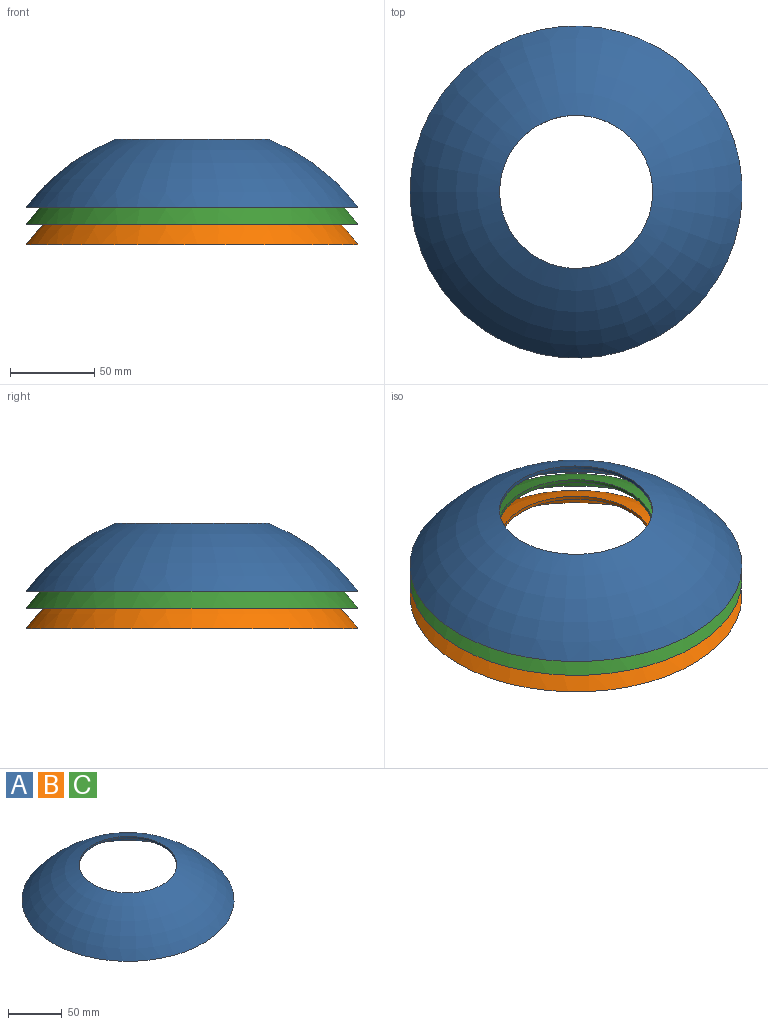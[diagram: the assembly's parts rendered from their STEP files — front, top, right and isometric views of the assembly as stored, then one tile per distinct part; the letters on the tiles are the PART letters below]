
ASSEMBLY  parts=3 mates=1
PART A: 4 faces, bbox 197.5x197.5x40.5 mm
  f0: cylinder r=45.5mm len=91mm, axis (0,0,-1), area 614.7mm2, adj f1,f3
  f1: torus R=1.06mm, axis (0,0,-1), area 31492.1mm2, adj f0,f2
  f2: plane 197.47x197.47mm, normal (0,0,-1), area 1538.4mm2, adj f1,f3
  f3: torus R=1.06mm, axis (0,0,-1), area 29338.7mm2, adj f0,f2
PART B: same geometry as A
PART C: same geometry as A
PLACE A t=(-7.23,-36.77,-128.68)mm
PLACE B t=(-7.23,-36.77,-150.78)mm
PLACE C t=(-7.23,-36.77,-138.68)mm
MATE cylindrical A.f0 <-> C.f0  axis (0,0,-1) through (-7.23,-36.77,-52.72)mm
